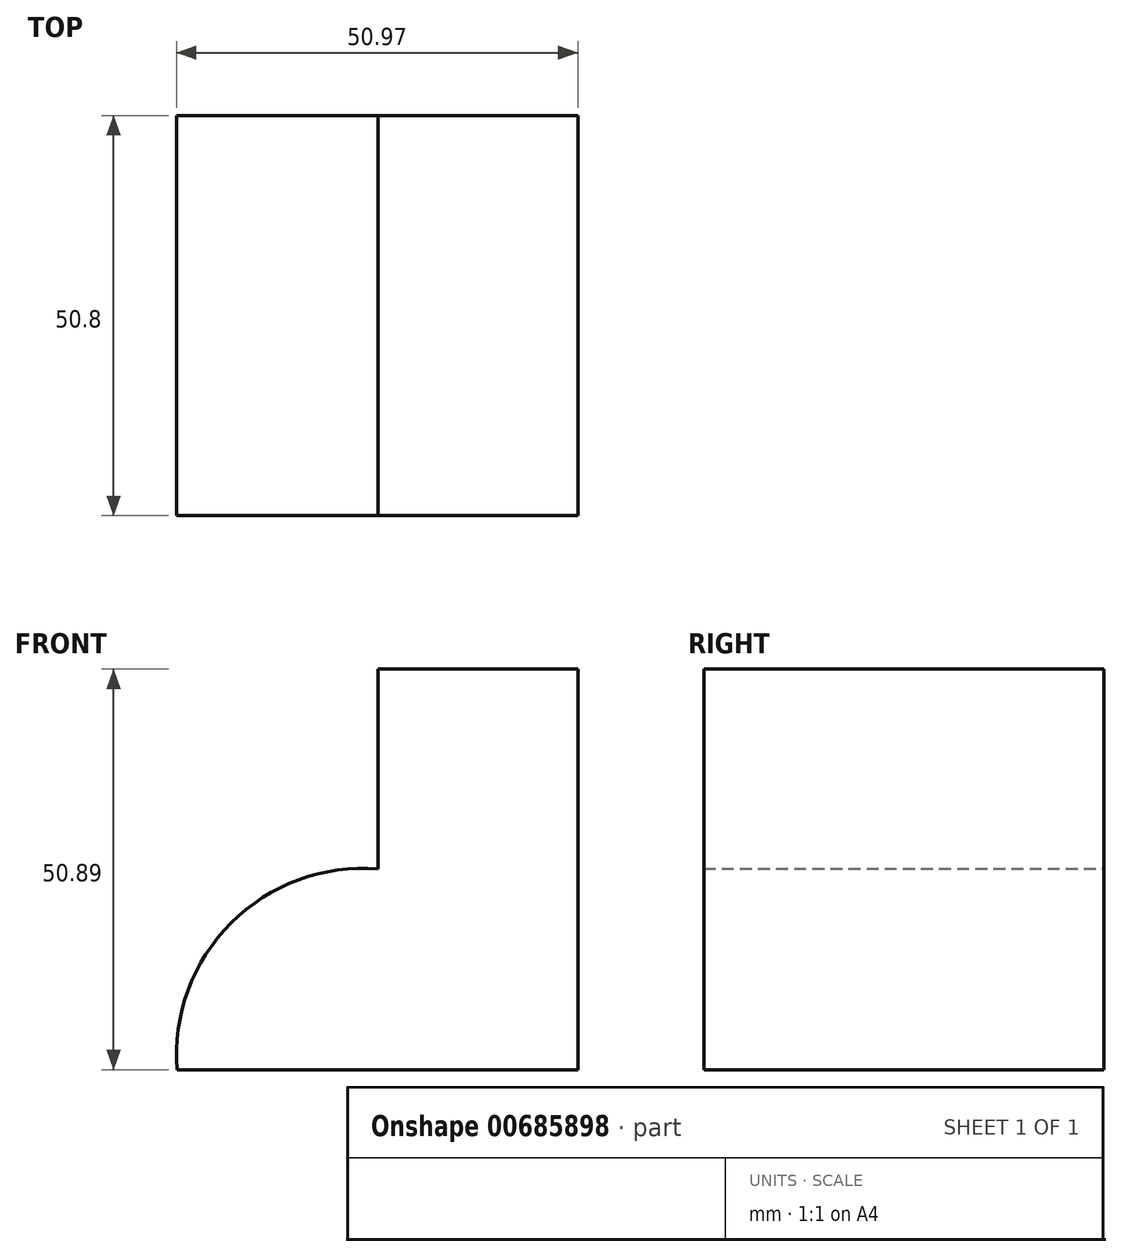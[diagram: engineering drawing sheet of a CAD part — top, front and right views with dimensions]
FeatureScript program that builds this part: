
annotation { "Feature Type Name" : "Feature", "Feature Type Description" : "" }
export const myFeature = defineFeature(function(context is Context, id is Id, definition is map)
    precondition{}
    {
        {
            var Q0;
            Q0=qCreatedBy(makeId("Front.planeOp"),FACE);
            var sketch = newSketch(context, id + "F0", { "sketchPlane" : qUnion([Q0])});
            skLineSegment(sketch, "E0", {"start": v(0, 0) * mm, "end": v(50.89, 0) * mm});
            skLineSegment(sketch, "E1", {"start": v(50.89, 0) * mm, "end": v(50.89, 50.89) * mm});
            skLineSegment(sketch, "E2", {"start": v(50.89, 50.89) * mm, "end": v(25.5, 50.89) * mm});
            skLineSegment(sketch, "E3", {"start": v(25.5, 50.89) * mm, "end": v(25.5, 25.5) * mm});
            skArc(sketch, "E4", {"start": v(25.5, 25.5) * mm, "mid": v(6.85, 18.64) * mm, "end": v(0, 0) * mm});
            skSolve(sketch);
        }
        {
            var Q0;
            Q0 = qSketchRegion(id + "F0", true);
            extrude(context, id + "F1", {"entities" : qUnion([Q0]), "depth" : 50.8 * mm, "offsetDistance" : 25.4 * mm});
        }
    });
